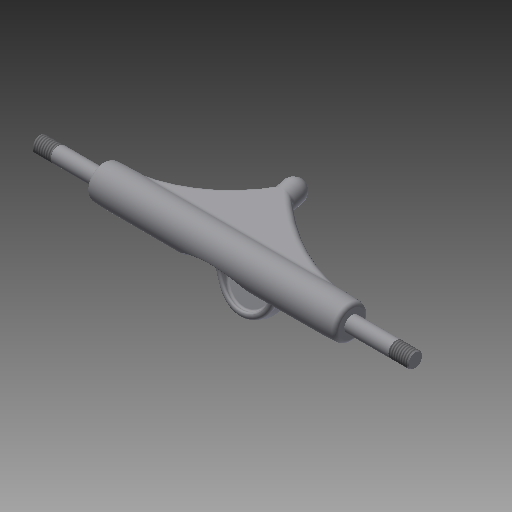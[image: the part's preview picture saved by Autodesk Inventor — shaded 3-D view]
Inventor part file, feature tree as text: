
AUTODESK INVENTOR PART (.ipt)
format: ipt  version: 2019 (Build 230136000, 136)  size: 1,439,744 bytes
history: native  units: mm
features: fillet x17, other x16, extrude x8, sketch x4, chamfer x2, loft x2, thread x1, mirror x1, revolve x1
ambient origin geometry x8: Origin, YZ Plane, XZ Plane, XY Plane, X Axis, Y Axis, Z Axis, Center Point
bodies: Solido1 (feature_tree)
feature tree (52):
  other  "Piano di lavoro10"
  extrude  "Estrusione10"  Depth=11.0mm
  other  "Asse di lavoro2"
  other  "Piano di lavoro14"
  extrude  "Estrusione11"  Depth=36.0mm TaperAngle=0.0deg
  other  "Piano di lavoro19"
  extrude  "Estrusione12"  Depth=130.0mm
  fillet  "Raccordo10"  Radius=29.0mm
  fillet  "Raccordo11"  Radius=5.5mm
  fillet  "Raccordo12"  [1 undecoded]
  chamfer  "Smusso3"  Distance=18.0mm
  fillet  "Raccordo13"  Radius=130.0mm
  extrude  "Estrusione15"  Depth=2.75mm
  thread  "Filettatura3"
  chamfer  "Smusso4"  Distance=2.0mm
  mirror  "Specchio6"
  other  "Piano di lavoro35"
  extrude  "Estrusione20"  Depth=3.0mm
  extrude  "Estrusione21"  Depth=8.0mm
  extrude  "Estrusione22"  Depth=2.0mm
  fillet  "Raccordo14"  Radius=8.0mm
  fillet  "Raccordo15"  Radius=33.0mm
  other  "Piano di lavoro39"
  sketch  "Schizzo66"
  other  "Asse di lavoro13"
  other  "Piano di lavoro40"
  loft  "Loft14"
  extrude  "Estrusione25"  Depth=0.5mm TaperAngle=45.0deg
  fillet  "Raccordo21"  Radius=24.0mm
  fillet  "Raccordo22"  Radius=3.0mm
  fillet  "Raccordo28"  Radius=30.0mm
  fillet  "Raccordo29"  Radius=5.0mm
  loft  "Loft16"
  revolve  "Rivoluzione3"
  fillet  "Raccordo31"  Radius=1.0mm
  fillet  "Raccordo34"  Radius=1.0mm
  fillet  "Raccordo35"  [1 undecoded]
  fillet  "Raccordo36"  [1 undecoded]
  fillet  "Raccordo37"  [1 undecoded]
  fillet  "Raccordo38"  Radius=2.0mm
  fillet  "Raccordo39"  Radius=2.0mm
  other  "Linea chiusa proiettata8"
  other  "Linea chiusa proiettata10"
  sketch  "Schizzo57"
  other  "Linea chiusa proiettata21"
  other  "Spigoli5"
  sketch  "Schizzo72"
  other  "Linea chiusa proiettata24"
  other  "Spigoli6"
  sketch  "Schizzo74"
  other  "Proietta spigoli di taglio11"
  other  "Proietta spigoli di taglio13"
note: 4 required parameter values undecoded (feature->parameter linkage not recoverable at this tier; creation-order binding heuristic only, values carry confidence <= 0.55)
